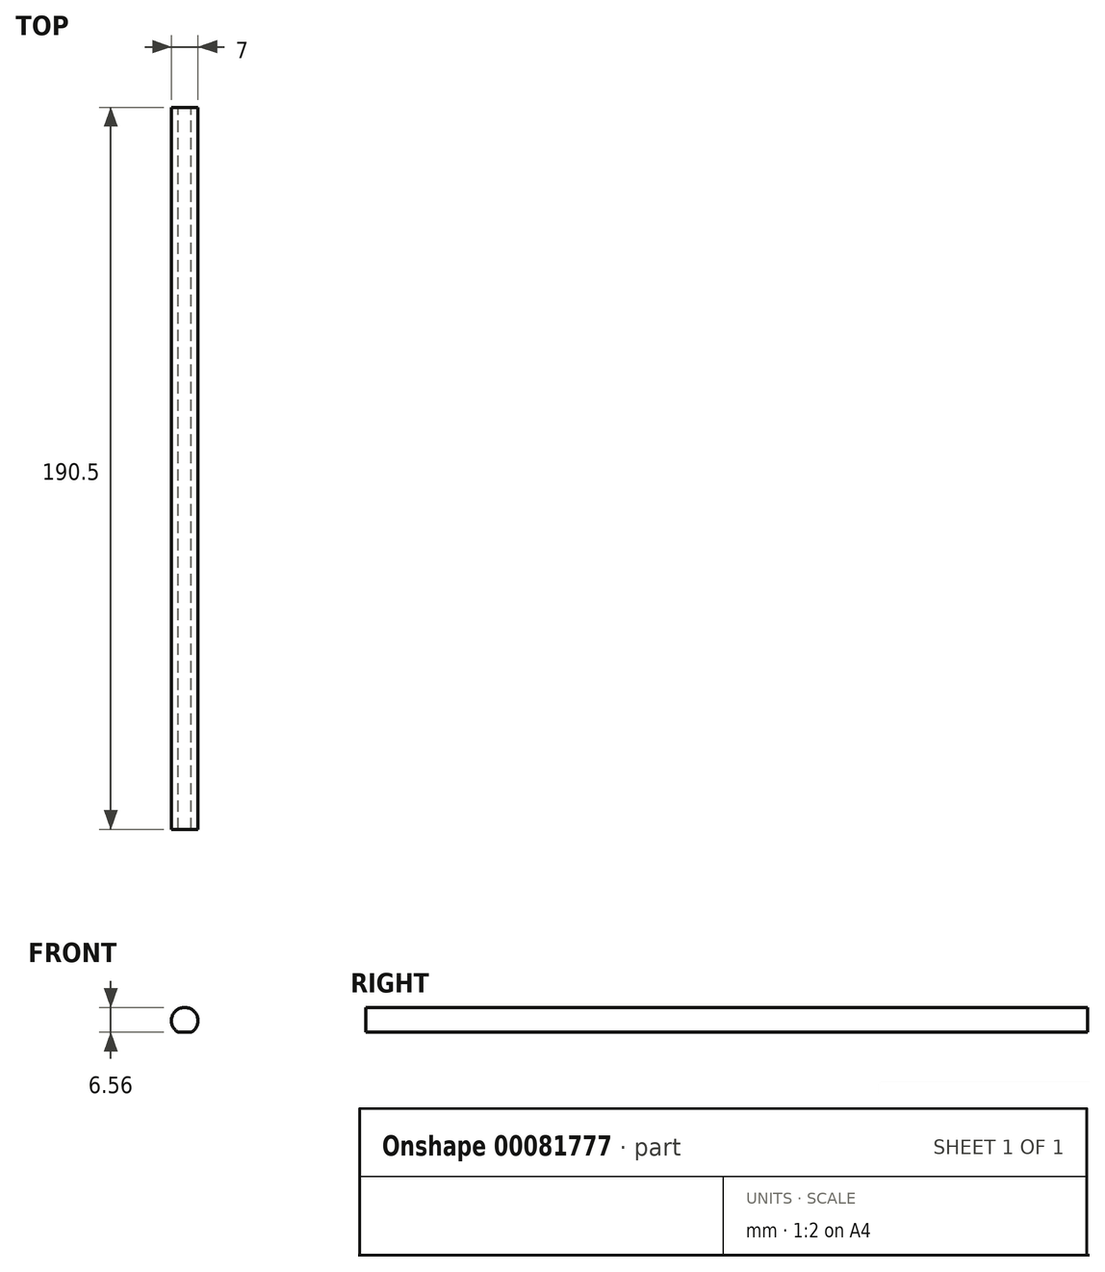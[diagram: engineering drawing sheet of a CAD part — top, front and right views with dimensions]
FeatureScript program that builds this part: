
annotation { "Feature Type Name" : "Feature", "Feature Type Description" : "" }
export const myFeature = defineFeature(function(context is Context, id is Id, definition is map)
    precondition{}
    {
        {
            var Q0;
            Q0=qCreatedBy(makeId("Front.planeOp"),FACE);
            var sketch = newSketch(context, id + "F0", { "sketchPlane" : qUnion([Q0])});
            skArc(sketch, "E0", {"start": v(1.7, -3.06) * mm, "mid": v(0, 3.5) * mm, "end": v(-1.7, -3.06) * mm});
            skLineSegment(sketch, "E1.bottom", {"start": v(-1.7, -3.06) * mm, "end": v(1.7, -3.06) * mm});
            skSolve(sketch);
        }
        {
            var Q0;
            Q0=makeQuery(id+"F0.imprint","IMPRINT",FACE,{"disambiguationData":[TD([[makeQuery(id+"F0.imprint","IMPRINT",EDGE,{"derivedFrom":sQuery(id+"F0.wireOp",EDGE,"E0")}),1.0]])]});
            var Q1;
            Q1=sQuery(id+"F0.wireOp",EDGE,"E0");
            extrude(context, id + "F1", {"entities" : qUnion([Q0]), "surfaceEntities" : qUnion([Q1]), "depth" : 190.5 * mm});
        }
    });
